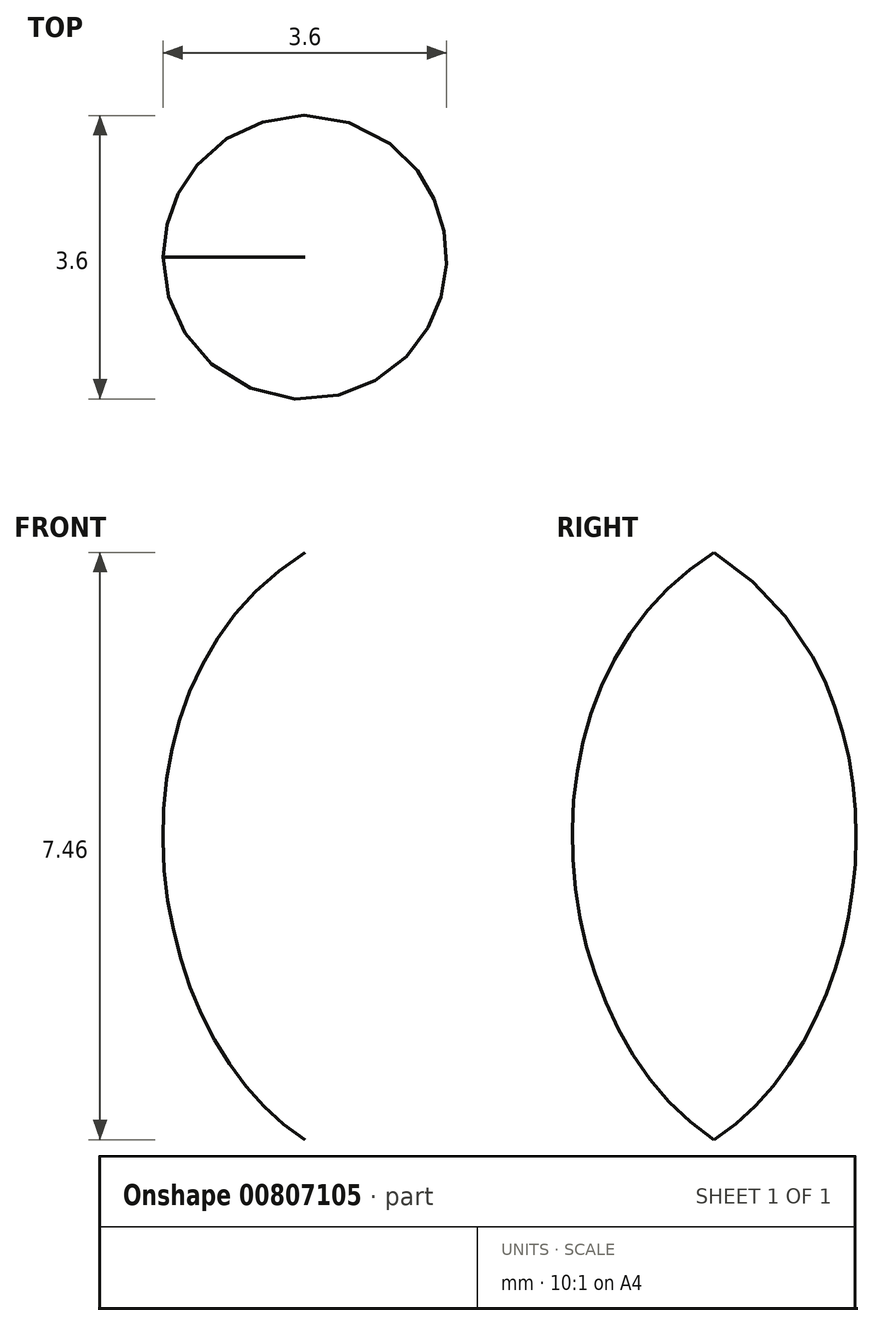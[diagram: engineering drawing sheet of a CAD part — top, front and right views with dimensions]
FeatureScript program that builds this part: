
annotation { "Feature Type Name" : "Feature", "Feature Type Description" : "" }
export const myFeature = defineFeature(function(context is Context, id is Id, definition is map)
    precondition{}
    {
        {
            var Q0;
            Q0=qCreatedBy(makeId("Front.planeOp"),FACE);
            var sketch = newSketch(context, id + "F0", { "sketchPlane" : qUnion([Q0])});
            skFitSpline(sketch, "E0", {"points": [v(33.52, 66.62) * mm, v(26.33, 51.6) * mm, v(39.94, 36.67) * mm, v(38.78, 1.61) * mm, v(17.84, 3.3) * mm, v(0, 0) * mm, v(0, 7.46) * mm, v(36.2, 6.14) * mm, v(36.74, 33.9) * mm, v(23.13, 50.28) * mm, v(28.3, 64.24) * mm, v(33.52, 66.62) * mm]});
            skLineSegment(sketch, "E1", {"start": v(0, 95.14) * mm, "end": v(0, -42.71) * mm});
            skSolve(sketch);
        }
        {
            var Q0;
            {var subQ0=sQuery(id+"F0.wireOp",EDGE,"E1");var subQ1=sQuery(id+"F0.wireOp",EDGE,"E0");var subQ2=makeQuery(id+"F0.imprint","INTERSECT",VERTEX,{"disambiguationData":[OD(0.0)],"derivedFrom":[subQ1,subQ0]});Q0=makeQuery(id+"F0.imprint","IMPRINT",FACE,{"disambiguationData":[TD([[makeQuery(id+"F0.imprint","IMPRINT",EDGE,{"disambiguationData":[TD([[subQ2,1.0]])],"derivedFrom":subQ1}),-1.0]])]});}
            var Q1;
            Q1=sQuery(id+"F0.wireOp",EDGE,"E1");
            revolve(context, id + "F1", {"surfaceOperationType" : NewSurfaceOperationType.NEW, "entities" : qUnion([Q0]), "axis" : qUnion([Q1]), "revolveType" : RevolveType.FULL});
        }
    });
